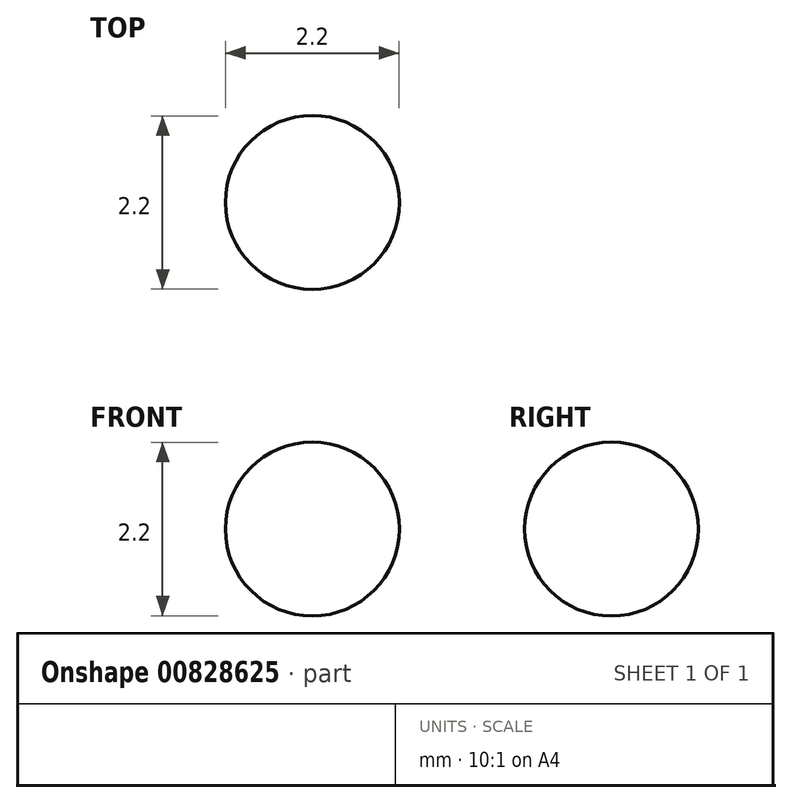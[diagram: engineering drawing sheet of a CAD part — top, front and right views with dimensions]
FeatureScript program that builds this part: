
annotation { "Feature Type Name" : "Feature", "Feature Type Description" : "" }
export const myFeature = defineFeature(function(context is Context, id is Id, definition is map)
    precondition{}
    {
        {
            var Q0;
            Q0=qCreatedBy(makeId("Front.planeOp"),FACE);
            var sketch = newSketch(context, id + "F0", { "sketchPlane" : qUnion([Q0])});
            skLineSegment(sketch, "E0", {"start": v(0, -1.1) * mm, "end": v(0, 1.1) * mm});
            skArc(sketch, "E1", {"start": v(0, -1.1) * mm, "mid": v(1.1, 0) * mm, "end": v(0, 1.1) * mm});
            skSolve(sketch);
        }
        {
            var Q0;
            Q0 = qSketchRegion(id + "F0", true);
            var Q1;
            Q1=sQuery(id+"F0.wireOp",EDGE,"E0");
            revolve(context, id + "F1", {"surfaceOperationType" : NewSurfaceOperationType.NEW, "entities" : qUnion([Q0]), "axis" : qUnion([Q1]), "revolveType" : RevolveType.FULL});
        }
    });
